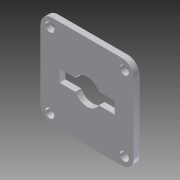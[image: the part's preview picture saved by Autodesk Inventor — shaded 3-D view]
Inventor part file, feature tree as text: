
AUTODESK INVENTOR PART (.ipt)
format: ipt  version: 2012 (Build 160160000, 160)  size: 183,296 bytes
history: native  units: in
note: dims shown in document units (in); Inventor stores cm internally (conversion verified against a paired STEP export)
features: extrude x5, fillet x3, sketch x1, hole x1
ambient origin geometry x8: Origin, YZ Plane, XZ Plane, XY Plane, X Axis, Y Axis, Z Axis, Center Point
bodies: Solid1 (feature_tree)
feature tree (10):
  sketch  "Sketch1"  dims[d0=0.9449in d1=0.4724in d2=1.0236in d3=0.5118in d4=0.0787in d5=0.2559in d6=0.128in d7=0.0787in d8=0.5625in d9=2.0in d10=1.0in d11=2.0in d12=1.0in d13=0.1181in d14=0.3937in d15=0.1575in d16=0.1575in d17=0.1575in d18=0.1575in d19=0.1575in d20=0.2in d21=0.2in d22=0.2in d23=0.2in d24=0.125in d25=0.0in d26=0.125in d34=1.6in d35=1.6in d44=0.25in d45=0.125in d46=0.0in d47=0.125in d48=0.0in d49=0.125in d50=0.0in d51=0.125in d52=0.0in d53=0.1935in d54=0.75in d55=0.375in d56=0.25in d57=0.5635in d58=1.0in d59=0.8108in d60=0.25in]
  extrude  "Extrusion1"  Depth=0.4724in
  fillet  "Fillet1"  Radius=1.0236in
  fillet  "Fillet2"  Radius=0.5118in
  extrude  "Extrusion2"  Depth=0.0787in
  extrude  "Extrusion3"  Depth=0.2559in
  extrude  "Extrusion4"  Depth=0.128in
  extrude  "Extrusion5"  Depth=0.0787in
  hole  "Hole2"  [1 undecoded]
  fillet  "Fillet3"  Radius=2.0in
note: 1 required parameter value undecoded (feature->parameter linkage not recoverable at this tier; creation-order binding heuristic only, values carry confidence <= 0.55)
